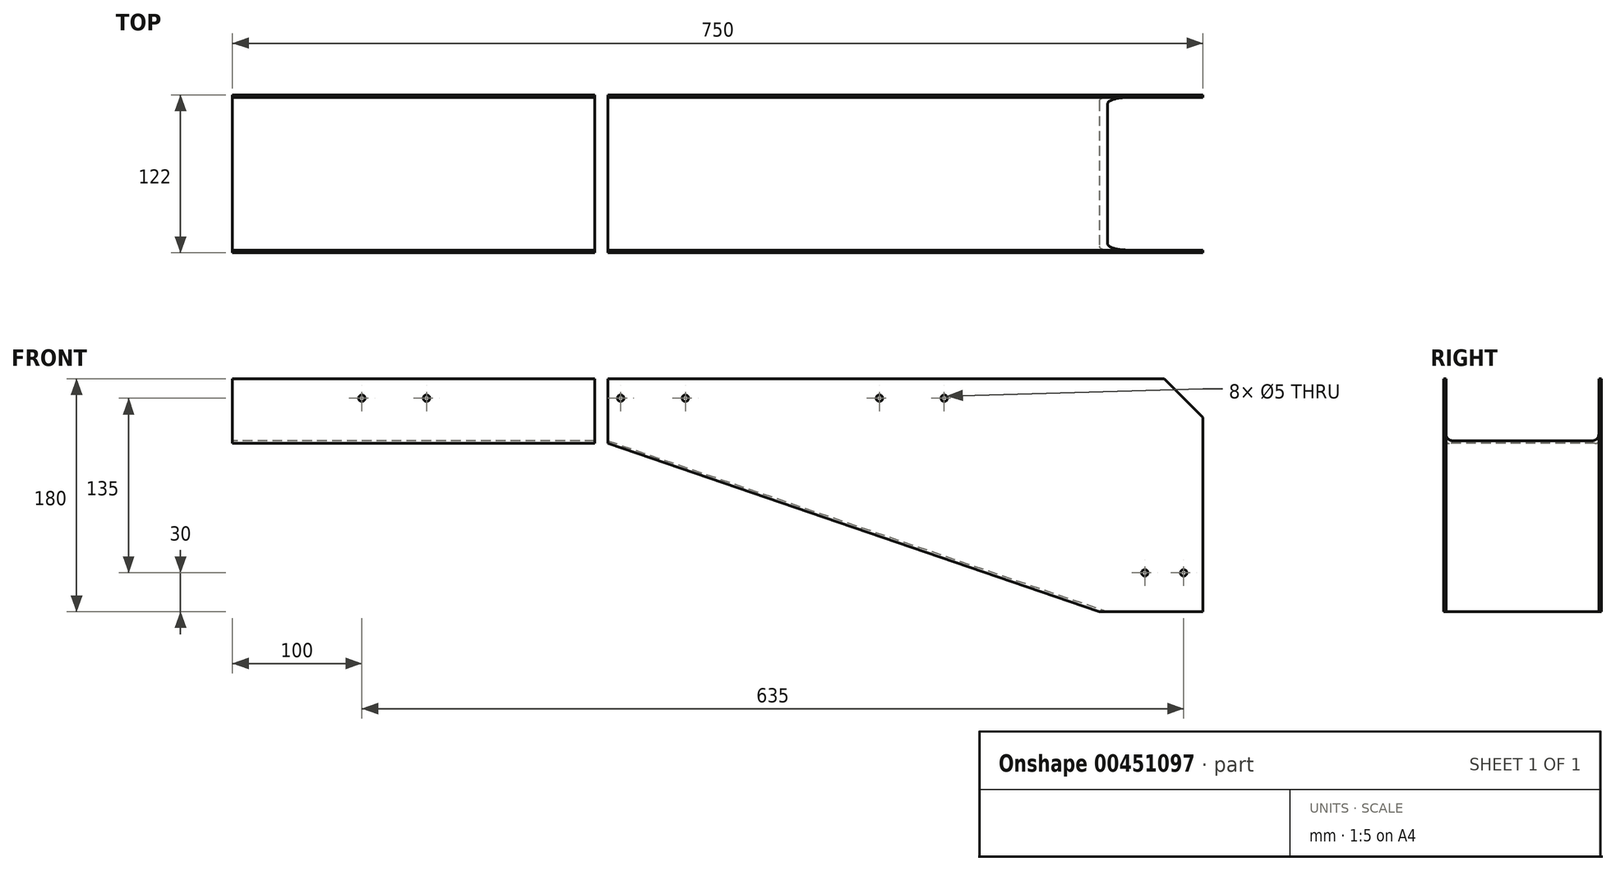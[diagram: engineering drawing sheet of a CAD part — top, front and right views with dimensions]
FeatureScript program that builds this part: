
annotation { "Feature Type Name" : "Feature", "Feature Type Description" : "" }
export const myFeature = defineFeature(function(context is Context, id is Id, definition is map)
    precondition{}
    {
        {
            var Q0;
            Q0=qCreatedBy(makeId("Front.planeOp"),FACE);
            var sketch = newSketch(context, id + "F0", { "sketchPlane" : qUnion([Q0])});
            skLineSegment(sketch, "E0", {"start": v(0, 0) * mm, "end": v(0, 180) * mm});
            skLineSegment(sketch, "E1", {"start": v(-760, 180) * mm, "end": v(-760, 130) * mm, "construction": true});
            skLineSegment(sketch, "E2", {"start": v(-760, 130) * mm, "end": v(-460, 130) * mm, "construction": true});
            skLineSegment(sketch, "E3", {"start": v(-460, 130) * mm, "end": v(-80, 0) * mm});
            skLineSegment(sketch, "E4", {"start": v(-80, 0) * mm, "end": v(0, 0) * mm});
            skLineSegment(sketch, "E5", {"start": v(-460, 130) * mm, "end": v(-460, 180) * mm});
            skLineSegment(sketch, "E6", {"start": v(-460, 180) * mm, "end": v(0, 180) * mm});
            skLineSegment(sketch, "E7", {"start": v(-460, 180) * mm, "end": v(-760, 180) * mm, "construction": true});
            skSolve(sketch);
        }
        {
            var Q0;
            Q0 = qSketchRegion(id + "F0", true);
            extrude(context, id + "F1", {"entities" : qUnion([Q0]), "oppositeDirection" : true, "depth" : 122 * mm, "offsetDistance" : 25 * mm});
        }
        {
            var Q0;
            Q0=makeQuery(id+"F1.opExtrude","SWEPT_FACE",FACE,{"disambiguationData":[OSD([sQuery(id+"F0.wireOp",EDGE,"E6")])]});
            var Q1;
            Q1=makeQuery(id+"F1.opExtrude","SWEPT_FACE",FACE,{"disambiguationData":[OSD([sQuery(id+"F0.wireOp",EDGE,"E0")])]});
            var Q2;
            Q2=makeQuery(id+"F1.opExtrude","SWEPT_FACE",FACE,{"disambiguationData":[OSD([sQuery(id+"F0.wireOp",EDGE,"E4")])]});
            var Q3;
            Q3=makeQuery(id+"F1.opExtrude","SWEPT_FACE",FACE,{"disambiguationData":[OSD([sQuery(id+"F0.wireOp",EDGE,"E5")])]});
            shell(context, id + "F2", {"entities" : qUnion([Q0, Q1, Q2, Q3]), "thickness" : 2 * mm});
        }
        {
            var Q0;
            Q0=makeQuery(id+"F1.opExtrude","CAP_EDGE",EDGE,{"disambiguationData":[OSD([sQuery(id+"F0.wireOp",EDGE,"E3")])],"isStart":true});
            var Q1;
            Q1=makeQuery(id+"F1.opExtrude","CAP_EDGE",EDGE,{"disambiguationData":[OSD([sQuery(id+"F0.wireOp",EDGE,"E3")])],"isStart":false});
            var Q2;
            {var subQ0=sQuery(id+"F0.wireOp",EDGE,"E3");Q2=makeQuery(id+"F2.opShell","OFFSET_EDGE",EDGE,{"disambiguationData":[OSD([subQ0]),TDD([makeQuery(id+"F1.opExtrude","CAP_EDGE",EDGE,{"disambiguationData":[OSD([subQ0])],"isStart":true})])]});}
            var Q3;
            {var subQ0=sQuery(id+"F0.wireOp",EDGE,"E3");Q3=makeQuery(id+"F2.opShell","OFFSET_EDGE",EDGE,{"disambiguationData":[OSD([subQ0]),TDD([makeQuery(id+"F1.opExtrude","CAP_EDGE",EDGE,{"disambiguationData":[OSD([subQ0])],"isStart":false})])]});}
            fillet(context, id + "F3", {"entities" : qUnion([Q0, Q1, Q2, Q3]), "radius" : 5 * mm, "tangentPropagation" : true, "allowEdgeOverflow" : false});
        }
        {
            var Q0;
            Q0=makeQuery(id+"F2.opShell","OFFSET_EDGE",EDGE,{"disambiguationData":[OSD([sQuery(id+"F0.wireOp",EDGE,"E0"),sQuery(id+"F0.wireOp",EDGE,"E6")])]});
            var Q1;
            Q1=makeQuery(id+"F1.opExtrude","SWEPT_EDGE",EDGE,{"disambiguationData":[OSD([sQuery(id+"F0.wireOp",EDGE,"E0"),sQuery(id+"F0.wireOp",EDGE,"E6")])]});
            chamfer(context, id + "F4", {"entities" : qUnion([Q0, Q1]), "width" : 30 * mm, "tangentPropagation" : true});
        }
        {
            var Q0;
            Q0=qCreatedBy(makeId("Front.planeOp"),FACE);
            var sketch = newSketch(context, id + "F5", { "sketchPlane" : qUnion([Q0])});
            skLineSegment(sketch, "E8.bottom", {"start": v(-470, 180) * mm, "end": v(-750, 180) * mm});
            skLineSegment(sketch, "E8.top", {"start": v(-470, 130) * mm, "end": v(-750, 130) * mm});
            skLineSegment(sketch, "E8.left", {"start": v(-470, 180) * mm, "end": v(-470, 130) * mm});
            skLineSegment(sketch, "E8.right", {"start": v(-750, 180) * mm, "end": v(-750, 130) * mm});
            skSolve(sketch);
        }
        {
            var Q0;
            Q0 = qSketchRegion(id + "F5", true);
            extrude(context, id + "F6", {"entities" : qUnion([Q0]), "oppositeDirection" : true, "depth" : 122 * mm, "offsetDistance" : 25 * mm});
        }
        {
            var Q0;
            Q0=makeQuery(id+"F6.opExtrude","SWEPT_FACE",FACE,{"disambiguationData":[OSD([sQuery(id+"F5.wireOp",EDGE,"E8.bottom")])]});
            var Q1;
            Q1=makeQuery(id+"F6.opExtrude","SWEPT_FACE",FACE,{"disambiguationData":[OSD([sQuery(id+"F5.wireOp",EDGE,"E8.left")])]});
            var Q2;
            Q2=makeQuery(id+"F6.opExtrude","SWEPT_FACE",FACE,{"disambiguationData":[OSD([sQuery(id+"F5.wireOp",EDGE,"E8.right")])]});
            shell(context, id + "F7", {"entities" : qUnion([Q0, Q1, Q2]), "thickness" : 2 * mm});
        }
        {
            var Q0;
            Q0=makeQuery(id+"F1.opExtrude","CAP_FACE",FACE,{"disambiguationData":[OSD([sQuery(id+"F0.wireOp",EDGE,"E0"),sQuery(id+"F0.wireOp",EDGE,"E3"),sQuery(id+"F0.wireOp",EDGE,"E4"),sQuery(id+"F0.wireOp",EDGE,"E5"),sQuery(id+"F0.wireOp",EDGE,"E6")])],"isStart":true});
            var sketch = newSketch(context, id + "F8", { "sketchPlane" : qUnion([Q0])});
            skCircle(sketch, "E9", {"center": v(-45, 30) * mm, "radius": 2.5 * mm});
            skCircle(sketch, "E10", {"center": v(-15, 30) * mm, "radius": 2.5 * mm});
            skCircle(sketch, "E11", {"center": v(-450, 165) * mm, "radius": 2.5 * mm});
            skCircle(sketch, "E12", {"center": v(-400, 165) * mm, "radius": 2.5 * mm});
            skCircle(sketch, "E13", {"center": v(-250, 165) * mm, "radius": 2.5 * mm});
            skCircle(sketch, "E14", {"center": v(-200, 165) * mm, "radius": 2.5 * mm});
            skCircle(sketch, "E15", {"center": v(-650, 165) * mm, "radius": 2.5 * mm});
            skCircle(sketch, "E16", {"center": v(-600, 165) * mm, "radius": 2.5 * mm});
            skSolve(sketch);
        }
        {
            var Q0;
            Q0 = qSketchRegion(id + "F8", true);
            extrude(context, id + "F9", {"entities" : qUnion([Q0]), "operationType" : NewBodyOperationType.REMOVE, "oppositeDirection" : true, "depth" : 25 * mm, "offsetDistance" : 25 * mm});
        }
        {
            var Q0;
            Q0=makeQuery(id+"F6.opExtrude","CAP_EDGE",EDGE,{"disambiguationData":[OSD([sQuery(id+"F5.wireOp",EDGE,"E8.top")])],"isStart":true});
            var Q1;
            Q1=makeQuery(id+"F6.opExtrude","CAP_EDGE",EDGE,{"disambiguationData":[OSD([sQuery(id+"F5.wireOp",EDGE,"E8.top")])],"isStart":false});
            var Q2;
            {var subQ0=sQuery(id+"F5.wireOp",EDGE,"E8.top");Q2=makeQuery(id+"F7.opShell","OFFSET_EDGE",EDGE,{"disambiguationData":[OSD([subQ0]),TDD([makeQuery(id+"F6.opExtrude","CAP_EDGE",EDGE,{"disambiguationData":[OSD([subQ0])],"isStart":false})])]});}
            var Q3;
            {var subQ0=sQuery(id+"F5.wireOp",EDGE,"E8.top");Q3=makeQuery(id+"F7.opShell","OFFSET_EDGE",EDGE,{"disambiguationData":[OSD([subQ0]),TDD([makeQuery(id+"F6.opExtrude","CAP_EDGE",EDGE,{"disambiguationData":[OSD([subQ0])],"isStart":true})])]});}
            fillet(context, id + "F10", {"entities" : qUnion([Q0, Q1, Q2, Q3]), "radius" : 5 * mm, "tangentPropagation" : true, "allowEdgeOverflow" : false});
        }
    });
